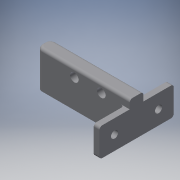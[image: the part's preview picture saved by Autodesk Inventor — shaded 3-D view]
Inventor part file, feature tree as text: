
AUTODESK INVENTOR PART (.ipt)
format: ipt  version: 2018 (Build 220112000, 112)  size: 228,352 bytes
history: native  units: mm
features: sketch x6, extrude x5, other x5, reference x4, fillet x2, plane x1, projected_geometry x1
ambient origin geometry x8: Origin, YZ Plane, XZ Plane, XY Plane, X Axis, Y Axis, Z Axis, Center Point
bodies: Solid1 (feature_tree)
feature tree (24):
  extrude  "Extrusion1"  Depth=10.0mm TaperAngle=0.0deg
  sketch  "Sketch2"  dims[d4=2.5mm d5=2.5mm]
  plane  "Work Plane1"
  extrude  "Extrusion2"  Depth=2.5mm
  extrude  "Extrusion3"  Depth=1.0mm
  fillet  "Fillet1"  Radius=3.0mm
  sketch  "Sketch4"  dims[d11=10.0mm d12=3.0mm]
  extrude  "Extrusion4"  Depth=10.0mm
  extrude  "Extrusion5"  Depth=3.0mm
  fillet  "Fillet2"  Radius=100.0mm
  sketch  "Sketch1"  dims[d0=10.0mm d1=0.0mm d2=10.0mm d3=0.0mm]
  reference  "Reference1"
  reference  "Reference2"
  reference  "Reference3"
  sketch  "Sketch3"  dims[d6=2.0mm d7=0.0mm d8=1.0mm d9=3.0mm d10=0.0mm]
  reference  "Reference4"
  sketch  "Sketch5"  dims[d13=9.5mm d14=3.0mm d15=100.0mm d16=0.0mm]
  projected_geometry  "Projected Loop1"
  sketch  "Sketch6"  dims[d17=1.0mm]
  other  "<userpath>\OneDrive\Documents\Inventor\TSA\2018\Animatronics\Tortoise\AssemblyTURTLE.iam"
  other  "AssemblyTURTLE.iam"
  other  "GuideArm:1"
  other  "Frame - Copy:1"
  other  "Supporter:1"
